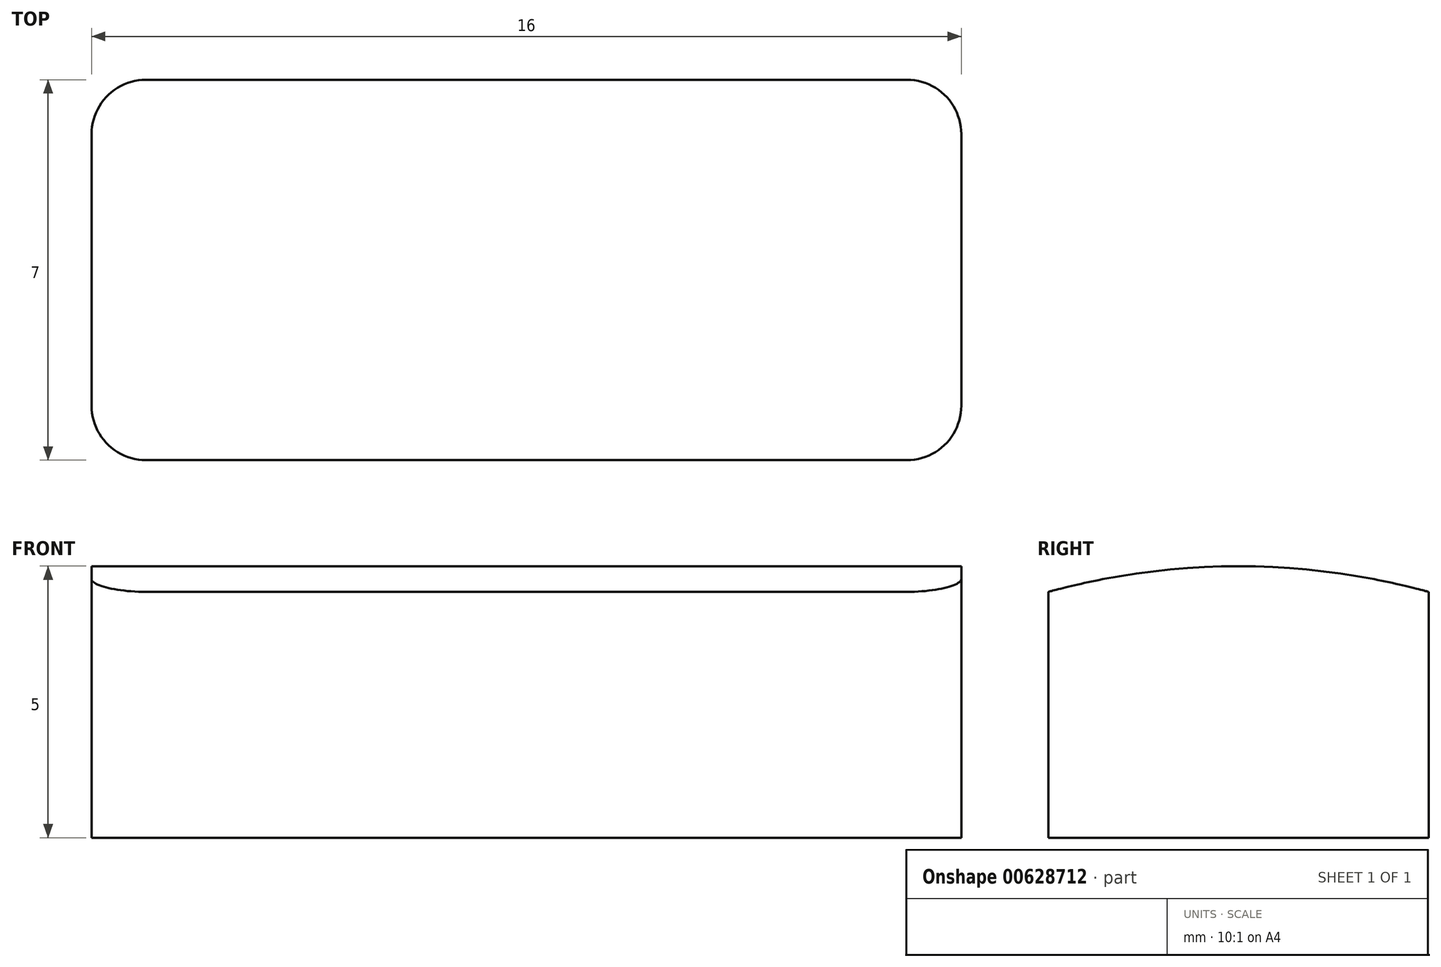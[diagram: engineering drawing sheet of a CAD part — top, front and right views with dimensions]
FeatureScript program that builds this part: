
annotation { "Feature Type Name" : "Feature", "Feature Type Description" : "" }
export const myFeature = defineFeature(function(context is Context, id is Id, definition is map)
    precondition{}
    {
        {
            var Q0;
            Q0=qCreatedBy(makeId("Right.planeOp"),FACE);
            var sketch = newSketch(context, id + "F0", { "sketchPlane" : qUnion([Q0])});
            skLineSegment(sketch, "E0.bottom", {"start": v(3.5, -2.26) * mm, "end": v(-3.5, -2.26) * mm});
            skLineSegment(sketch, "E0.top", {"start": v(3.5, 2.26) * mm, "end": v(-3.5, 2.26) * mm, "construction": true});
            skLineSegment(sketch, "E0.left", {"start": v(3.5, -2.26) * mm, "end": v(3.5, 2.26) * mm});
            skLineSegment(sketch, "E0.right", {"start": v(-3.5, -2.26) * mm, "end": v(-3.5, 2.26) * mm});
            skPoint(sketch, "E0.middle", {"position": v(0, 0) * mm});
            skArc(sketch, "E1", {"start": v(3.5, 2.26) * mm, "mid": v(0, 2.74) * mm, "end": v(-3.5, 2.26) * mm});
            skSolve(sketch);
        }
        {
            var Q0;
            Q0=qSketchRegion(id+"F0",true);
            extrude(context, id + "F1", {"entities" : qUnion([Q0]), "endBound" : BoundingType.SYMMETRIC, "depth" : 16 * mm, "offsetDistance" : 25 * mm});
        }
        {
            var Q0;
            Q0=makeQuery(id+"F1.opExtrude","CAP_EDGE",EDGE,{"disambiguationData":[OSD([sQuery(id+"F0.wireOp",EDGE,"E0.right")])],"isStart":false});
            var Q1;
            Q1=makeQuery(id+"F1.opExtrude","CAP_EDGE",EDGE,{"disambiguationData":[OSD([sQuery(id+"F0.wireOp",EDGE,"E0.right")])],"isStart":true});
            var Q2;
            Q2=makeQuery(id+"F1.opExtrude","CAP_EDGE",EDGE,{"disambiguationData":[OSD([sQuery(id+"F0.wireOp",EDGE,"E0.left")])],"isStart":false});
            var Q3;
            Q3=makeQuery(id+"F1.opExtrude","CAP_EDGE",EDGE,{"disambiguationData":[OSD([sQuery(id+"F0.wireOp",EDGE,"E0.left")])],"isStart":true});
            fillet(context, id + "F2", {"entities" : qUnion([Q0, Q1, Q2, Q3]), "radius" : 1 * mm, "tangentPropagation" : true, "allowEdgeOverflow" : false});
        }
    });
